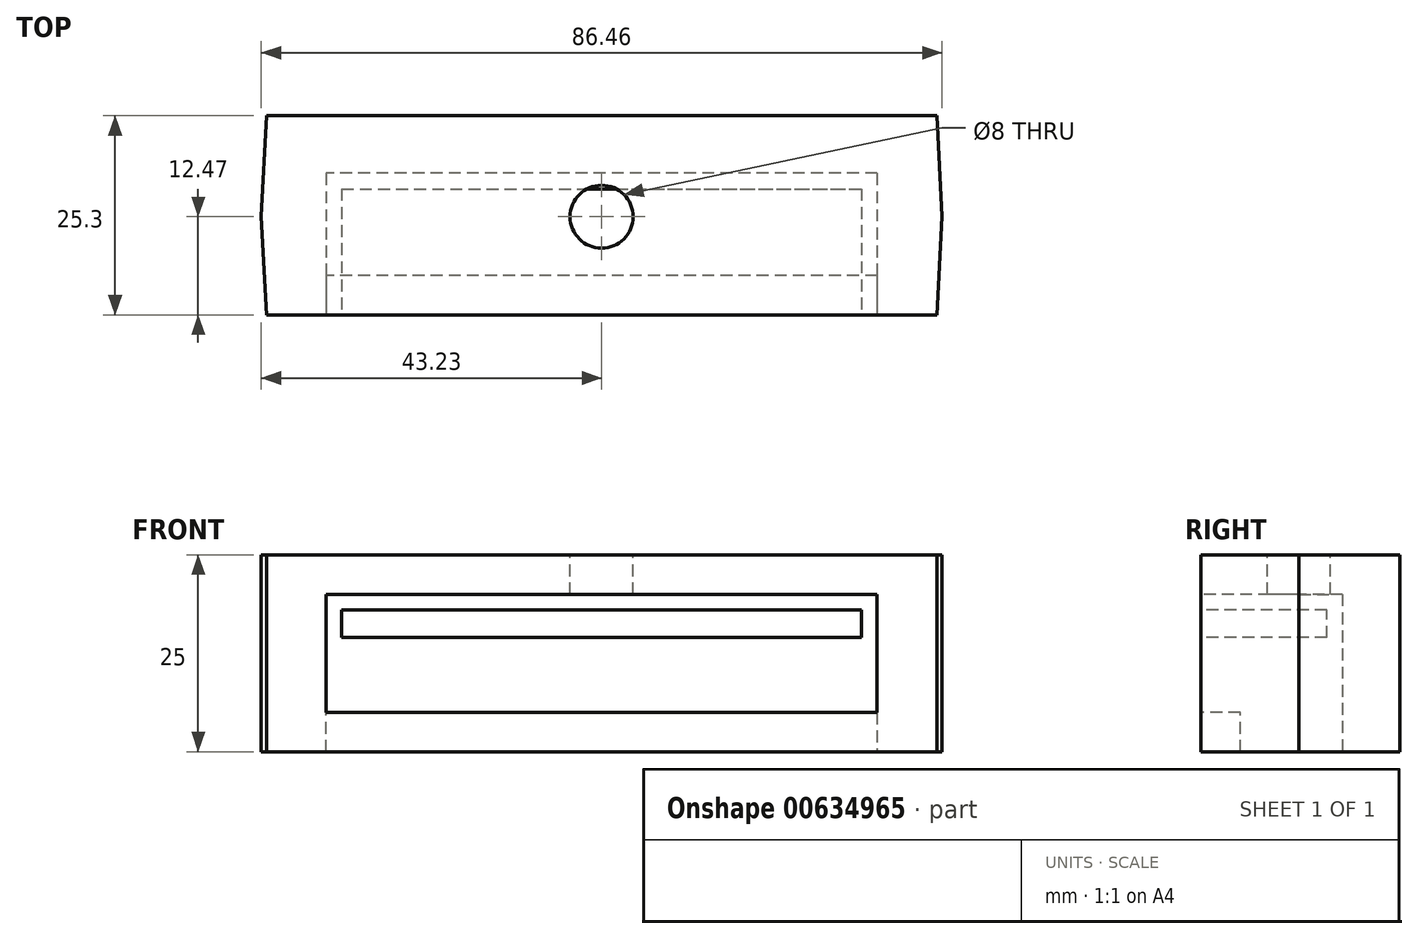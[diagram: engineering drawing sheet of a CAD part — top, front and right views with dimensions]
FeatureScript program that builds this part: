
annotation { "Feature Type Name" : "Feature", "Feature Type Description" : "" }
export const myFeature = defineFeature(function(context is Context, id is Id, definition is map)
    precondition{}
    {
        {
            var Q0;
            Q0=qCreatedBy(makeId("Top.planeOp"),FACE);
            var sketch = newSketch(context, id + "F0", { "sketchPlane" : qUnion([Q0])});
            skLineSegment(sketch, "E0", {"start": v(-43.23, 0) * mm, "end": v(43.23, 0) * mm, "construction": true});
            skLineSegment(sketch, "E1", {"start": v(0, -12.47) * mm, "end": v(0, 12.83) * mm, "construction": true});
            skLineSegment(sketch, "E2", {"start": v(-42.58, 12.83) * mm, "end": v(42.58, 12.83) * mm});
            skLineSegment(sketch, "E3", {"start": v(-42.58, -12.47) * mm, "end": v(42.58, -12.47) * mm});
            skLineSegment(sketch, "E4", {"start": v(-43.23, 0) * mm, "end": v(-42.58, -12.47) * mm});
            skLineSegment(sketch, "E5", {"start": v(-42.58, 12.83) * mm, "end": v(-43.23, 0) * mm});
            skLineSegment(sketch, "E6", {"start": v(42.58, 12.83) * mm, "end": v(43.23, 0) * mm});
            skLineSegment(sketch, "E7", {"start": v(43.23, 0) * mm, "end": v(42.58, -12.47) * mm});
            skSolve(sketch);
        }
        {
            var Q0;
            Q0 = qSketchRegion(id + "F0", true);
            extrude(context, id + "F1", {"entities" : qUnion([Q0]), "depth" : 25 * mm, "offsetDistance" : 25 * mm});
        }
        {
            var Q0;
            Q0=makeQuery(id+"F1.opExtrude","SWEPT_FACE",FACE,{"disambiguationData":[OSD([sQuery(id+"F0.wireOp",EDGE,"E3")])]});
            var sketch = newSketch(context, id + "F2", { "sketchPlane" : qUnion([Q0])});
            skLineSegment(sketch, "E8", {"start": v(0, 20) * mm, "end": v(35, 20) * mm});
            skLineSegment(sketch, "E9", {"start": v(35, 20) * mm, "end": v(35, 5) * mm});
            skLineSegment(sketch, "E10", {"start": v(35, 5) * mm, "end": v(-35, 5) * mm});
            skLineSegment(sketch, "E11", {"start": v(0, 20) * mm, "end": v(-35, 20) * mm});
            skLineSegment(sketch, "E12", {"start": v(-35, 20) * mm, "end": v(-35, 5) * mm});
            skSolve(sketch);
        }
        {
            var Q0;
            Q0 = qSketchRegion(id + "F2", true);
            extrude(context, id + "F3", {"entities" : qUnion([Q0]), "operationType" : NewBodyOperationType.REMOVE, "oppositeDirection" : true, "depth" : 18 * mm, "offsetDistance" : 25 * mm});
        }
        {
            var Q0;
            Q0=makeQuery(id+"F3.boolean.opBoolean","COPY",FACE,{"derivedFrom":makeQuery(id+"F3.opExtrude","SWEPT_FACE",FACE,{"disambiguationData":[OSD([sQuery(id+"F2.wireOp",EDGE,"E10")])]})});
            var sketch = newSketch(context, id + "F4", { "sketchPlane" : qUnion([Q0])});
            skPoint(sketch, "E13.endSnap0", {"position": v(0, -12.47) * mm});
            skLineSegment(sketch, "E14", {"start": v(0, -7.47) * mm, "end": v(-35, -7.47) * mm});
            skLineSegment(sketch, "E15", {"start": v(0, -7.47) * mm, "end": v(35, -7.47) * mm});
            skSolve(sketch);
        }
        {
            var Q0;
            Q0 = qSketchRegion(id + "F4", true);
            var Q1;
            {var subQ4=sQuery(id+"F4.wireOp",EDGE,"E14");Q1=makeQuery(id+"F4.imprint","IMPRINT",FACE,{"disambiguationData":[TD([[makeQuery(id+"F4.imprint","IMPRINT",EDGE,{"derivedFrom":subQ4}),-1.0]])]});}
            extrude(context, id + "F5", {"entities" : qUnion([Q0, Q1]), "operationType" : NewBodyOperationType.REMOVE, "oppositeDirection" : true, "depth" : 4.13 * mm, "offsetDistance" : 25 * mm});
        }
        {
            var Q0;
            Q0=makeQuery(id+"F1.opExtrude","CAP_FACE",FACE,{"disambiguationData":[OSD([sQuery(id+"F0.wireOp",EDGE,"E2"),sQuery(id+"F0.wireOp",EDGE,"E3"),sQuery(id+"F0.wireOp",EDGE,"E4"),sQuery(id+"F0.wireOp",EDGE,"E5"),sQuery(id+"F0.wireOp",EDGE,"E6"),sQuery(id+"F0.wireOp",EDGE,"E7")])],"isStart":false});
            var sketch = newSketch(context, id + "F6", { "sketchPlane" : qUnion([Q0])});
            skCircle(sketch, "E16", {"center": v(0, 0) * mm, "radius": 4 * mm});
            skSolve(sketch);
        }
        {
            var Q0;
            Q0 = qSketchRegion(id + "F6", true);
            extrude(context, id + "F7", {"entities" : qUnion([Q0]), "operationType" : NewBodyOperationType.REMOVE, "oppositeDirection" : true, "depth" : 9 * mm, "offsetDistance" : 25 * mm});
        }
        {
            var Q0;
            Q0=makeQuery(id+"F5.boolean.opBoolean","COPY",FACE,{"derivedFrom":makeQuery(id+"F5.opExtrude","CAP_FACE",FACE,{"disambiguationData":[OSD([sQuery(id+"F2.wireOp",EDGE,"E9"),sQuery(id+"F2.wireOp",EDGE,"E10"),sQuery(id+"F2.wireOp",EDGE,"E12"),sQuery(id+"F4.wireOp",EDGE,"E14"),sQuery(id+"F4.wireOp",EDGE,"E15")])],"isStart":false})});
            var sketch = newSketch(context, id + "F8", { "sketchPlane" : qUnion([Q0])});
            skSolve(sketch);
        }
        {
            var Q0;
            Q0 = qSketchRegion(id + "F8", true);
            var Q1;
            {var subQ0=sQuery(id+"F2.wireOp",EDGE,"E10");Q1=makeQuery(id+"F8.imprint","IMPRINT",FACE,{"disambiguationData":[TD([[makeQuery(id+"F8.imprint","IMPRINT",EDGE,{"derivedFrom":makeQuery(id+"F5.boolean.opBoolean","COPY",EDGE,{"derivedFrom":makeQuery(id+"F5.opExtrude","CAP_EDGE",EDGE,{"disambiguationData":[OSD([subQ0])],"isStart":false})})}),1.0]])]});}
            extrude(context, id + "F9", {"entities" : qUnion([Q0, Q1]), "operationType" : NewBodyOperationType.REMOVE, "oppositeDirection" : true, "depth" : 25 * mm, "offsetDistance" : 25 * mm});
        }
        {
            var Q0;
            Q0=makeQuery(id+"F1.opExtrude","SWEPT_FACE",FACE,{"disambiguationData":[OSD([sQuery(id+"F0.wireOp",EDGE,"E3")])]});
            var sketch = newSketch(context, id + "F10", { "sketchPlane" : qUnion([Q0])});
            skLineSegment(sketch, "E17", {"start": v(33, 16.4) * mm, "end": v(35, 16.4) * mm});
            skLineSegment(sketch, "E18", {"start": v(35, 16.4) * mm, "end": v(33, 16.4) * mm});
            skPoint(sketch, "E19.orphan", {"position": v(-33, 16.4) * mm});
            skLineSegment(sketch, "E20.bottom", {"start": v(-33, 14.5) * mm, "end": v(33, 14.5) * mm});
            skLineSegment(sketch, "E20.top", {"start": v(-33, 18) * mm, "end": v(33, 18) * mm});
            skLineSegment(sketch, "E20.left", {"start": v(-33, 14.5) * mm, "end": v(-33, 18) * mm});
            skLineSegment(sketch, "E20.right", {"start": v(33, 14.5) * mm, "end": v(33, 18) * mm});
            skSolve(sketch);
        }
        {
            var Q0;
            Q0 = qSketchRegion(id + "F10", true);
            extrude(context, id + "F11", {"entities" : qUnion([Q0]), "oppositeDirection" : true, "depth" : 16 * mm, "offsetDistance" : 25 * mm});
        }
    });
